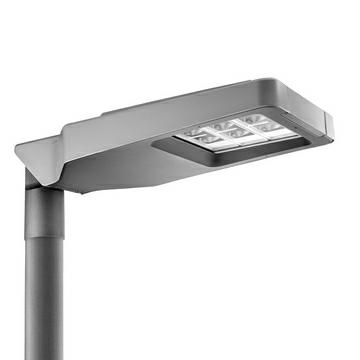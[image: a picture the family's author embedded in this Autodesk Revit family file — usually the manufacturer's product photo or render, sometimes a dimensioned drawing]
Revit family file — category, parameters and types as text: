
# Revit family: Lighting-Stradale-GEWISS-ROAD[5]MINI-LED_OTTICA_HUGE_CLII
name_source: partatom
category: Apparecchi per illuminazione
units: mm (PartAtom-declared; Revit-internal decimal feet)

## family parameters
Basato su piano di lavoro = No
Condiviso = No
Punto di calcolo locali = No
Quota connettore circolare = Usa diametro
Sempre verticale = Sì
Sorgente d'illuminazione = No
Taglio con vuoti quando caricato = No
Tipo di parte = Normale

## types (1)
- Lighting-Stradale-GEWISS-ROAD[5]MINI-LED_OTTICA_HUGE_CLII
    Alimentatore = Incluso
    Apparecchio a ridotta temperatura superficiale = -
    Applicazione = Esterno
    Cablaggio = Sezionatore
    Caratteristiche elettriche e gestione della luce = -
    Caratteristiche ottiche e illuminotecniche = -
    Carico apparente = 53 VA
    Catalogo = LIGHTING
    Catalogo Serie = ROAD [5]
    Certificazione DIN 18032-3 = -
    Certificazioni e classificazioni = -
    Classe fotobiologica = RG0
    Classe isolamento = II
    Classificazione: = -
    Codice Electrocod = 244C
    Codice digitale univoco (Datamatrix) = Attualmente non presente
    Colore = Grigio grafite
    Commenti sul wattaggio = 53W
    Contesto = Illuminazione stradale e parcheggi
    Controllo abbagliamento e luminanza = G*3 - ULOR = 0
    Corpo = Alluminio pressofuso
    Corrente di pilotaggio. = 0,7A
    Descrizione = GWR5172V - ROAD5 MINI HUGE V 2M 4000K 0,7A CL2
    Dispositivo di protezione = DM 10KV / CM 10KV
    Distanza minima dall'oggetto illuminato = 1M
    Durata di vita = L90B10 (Tq+25°C) = 100.000 h - L90B10 (Tq+50°C) = 75.000 h
    Efficienza luminosa (lm/W) = 111
    Finitura colore = Verniciato a polveri
    Fissaggio = Testa palo - Sbraccio
    Flusso nominale (lm) = 6240
    Frequenza nominale (Hz) = 50 / 60
    Gancio di chiusura = Maniglia frontale integrata
    Garanzia = 5 anni
    Grado di protezione = IP66
    Gruppo ottico = Riflettore in PC metallizzato
    Guarnizioni = silicone antinvecchiamento
    IDF = 6aaf7162-5e1f-4df8-ab3a-61c271de0dd2
    IDT = 71f3a6385bd246d58e1a34223c0a3191
    IPEA = STRADALE = A4+ // GRANDI AREE = A4+ // CICLOPEDONALI = A3+ // AREE VERDI = A3+ // CENTRO STORICO = A6+
    Immagine tipo = GWR5276M.jpg
    Inclinazione = -20° ÷ +10° sbraccio - -10° ÷ +20° testa palo
    Indice di resa cromatica = CRI-70
    Informazioni generali = -
    Installazione e manutenzione = -
    LED Life Time (L80B05) = 120000H
    Lampada = LED
    Lampada: = LED
    Lumen output (lm) = 6000
    Materiali = -
    Modello = GWR5172V
    Norma di riferimento = EN 60598-2-3, EN 60598-1 IEC/TR 62778
    Numero moduli = 2 (2x3 LED)
    Ottica = HUGE
    Peso (kg): = 6,6
    Potenza assorbita : = 54 W @ 0.7A
    Potenza di sistema = 53W
    Produttore = GEWISS S.p.A.
    Regolazione inclinazione = -20° ÷ +10° sbraccio - -10° ÷ +20° testa palo
    Resistenza agli urti = IK08
    Resistenza al filo incandescente = -
    SEO = Stradale
    Scheda Tecnica = https://www.gewiss.com
    Schermo = Vetro piano temperato spessore 4mm
    Sistema di controllo = DALI - 5 Step
    Sostituibilità gruppo ottico = Non disponibile
    Sostituibilità piastra di cablaggio = Non disponibile
    Superficie massima esposta al vento = 0,149999999999999M2
    Superficie massima esposta al vento : = 0,15 m²
    Temperatura di colore = 4000K
    Temperatura di colore: = 4000 K (CRI>70)
    Temperatura di esercizio = -25 +50 °C
    Temperatura di stoccaggio = -
    Temperatura di utilizzo = -25 +40 °C
    Tensione = 220/240 V - 50/60 Hz - Stand alone e/o Programmabile
    Tensione di alimentazione = 220 - 240 V
    Tipo di apparecchio = Apparecchiatura stradale a LED
    Tipo di installazione e montaggio = Testa palo - Sbraccio
    Tipologia = Programmabile (5 passi)
    Tipologia sorgente luminosa = LED - Non sostituibile
    Tolleranza cromatica = SDCM = 5
    URL = https://www.gewiss.com
    Vano di alimentazione = Integrato
    Versione file RFA = 20.11
    Viti esterne = Acciaio inox
